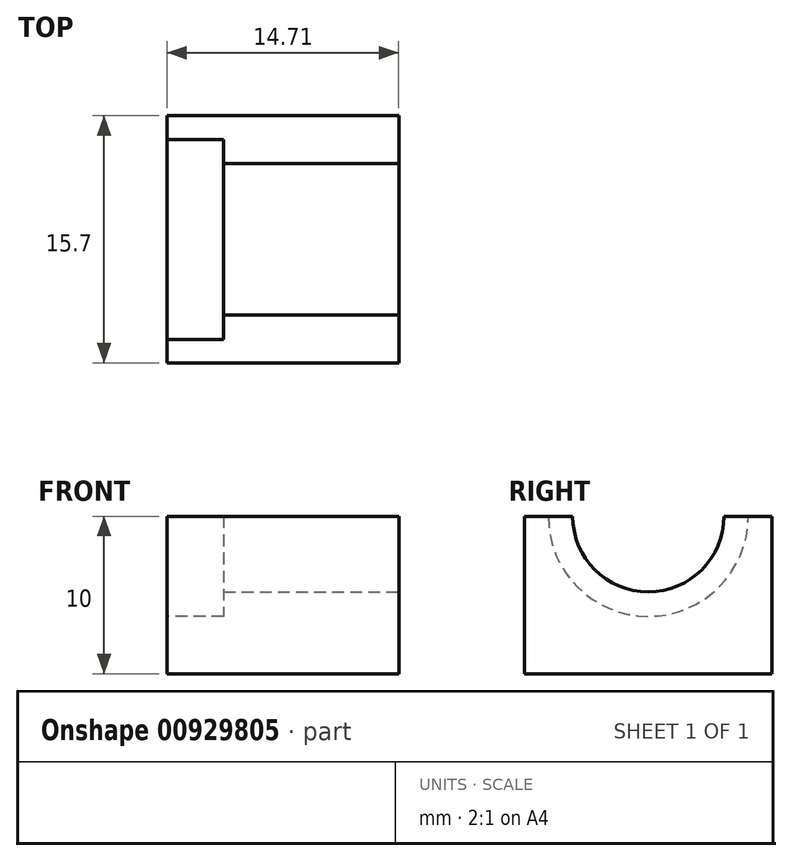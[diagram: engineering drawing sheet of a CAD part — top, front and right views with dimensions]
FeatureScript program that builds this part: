
annotation { "Feature Type Name" : "Feature", "Feature Type Description" : "" }
export const myFeature = defineFeature(function(context is Context, id is Id, definition is map)
    precondition{}
    {
        {
            var Q0;
            Q0=qCreatedBy(makeId("Front.planeOp"),FACE);
            var sketch = newSketch(context, id + "F0", { "sketchPlane" : qUnion([Q0])});
            skLineSegment(sketch, "E0", {"start": v(0, 0) * mm, "end": v(12.71, 0) * mm});
            skLineSegment(sketch, "E1", {"start": v(12.71, 0) * mm, "end": v(12.71, 20) * mm, "construction": true});
            skLineSegment(sketch, "E2", {"start": v(12.71, 20) * mm, "end": v(0, 20) * mm});
            skLineSegment(sketch, "E3", {"start": v(0, 20) * mm, "end": v(0, 17.5) * mm});
            skLineSegment(sketch, "E4", {"start": v(0, 17.5) * mm, "end": v(11.46, 17.5) * mm});
            skLineSegment(sketch, "E5", {"start": v(11.46, 17.5) * mm, "end": v(11.46, 2.5) * mm});
            skLineSegment(sketch, "E6", {"start": v(11.46, 2.5) * mm, "end": v(0, 2.5) * mm});
            skLineSegment(sketch, "E7", {"start": v(0, 2.5) * mm, "end": v(0, 0) * mm});
            skLineSegment(sketch, "E8.MirrorCS", {"start": v(12.71, 20) * mm, "end": v(25.43, 20) * mm});
            skLineSegment(sketch, "E9.MirrorCS", {"start": v(25.43, 20) * mm, "end": v(25.43, 17.5) * mm});
            skLineSegment(sketch, "E10.MirrorCS", {"start": v(25.43, 17.5) * mm, "end": v(13.96, 17.5) * mm});
            skLineSegment(sketch, "E11.MirrorCS", {"start": v(13.96, 17.5) * mm, "end": v(13.96, 2.5) * mm});
            skLineSegment(sketch, "E12.MirrorCS", {"start": v(13.96, 2.5) * mm, "end": v(25.43, 2.5) * mm});
            skLineSegment(sketch, "E13.MirrorCS", {"start": v(25.43, 2.5) * mm, "end": v(25.43, 0) * mm});
            skLineSegment(sketch, "E14.MirrorCS", {"start": v(25.43, 0) * mm, "end": v(12.71, 0) * mm});
            skSolve(sketch);
        }
        {
            var Q0;
            Q0=makeQuery(id+"F0.imprint","IMPRINT",FACE,{"disambiguationData":[TD([[makeQuery(id+"F0.imprint","IMPRINT",EDGE,{"derivedFrom":sQuery(id+"F0.wireOp",EDGE,"E0")}),1.0]])]});
            extrude(context, id + "F1", {"entities" : qUnion([Q0]), "oppositeDirection" : true, "depth" : 145 * mm, "offsetDistance" : 25 * mm});
        }
        {
            var Q0;
            Q0=makeQuery(id+"F1.opExtrude","SWEPT_FACE",FACE,{"disambiguationData":[OSD([sQuery(id+"F0.wireOp",EDGE,"E11.MirrorCS")])]});
            var sketch = newSketch(context, id + "F2", { "sketchPlane" : qUnion([Q0])});
            skLineSegment(sketch, "E15.bottom", {"start": v(0, 17.5) * mm, "end": v(15.7, 17.5) * mm});
            skLineSegment(sketch, "E15.top", {"start": v(0, 2.5) * mm, "end": v(15.7, 2.5) * mm});
            skLineSegment(sketch, "E15.left", {"start": v(0, 17.5) * mm, "end": v(0, 2.5) * mm});
            skLineSegment(sketch, "E15.right", {"start": v(15.7, 17.5) * mm, "end": v(15.7, 2.5) * mm});
            skSolve(sketch);
        }
        {
            var Q0;
            Q0=makeQuery(id+"F2.imprint","IMPRINT",FACE,{"disambiguationData":[TD([[makeQuery(id+"F2.imprint","IMPRINT",EDGE,{"derivedFrom":sQuery(id+"F2.wireOp",EDGE,"E15.bottom")}),1.0]])]});
            var Q1;
            Q1=makeQuery(id+"F1.opExtrude","SWEPT_FACE",FACE,{"disambiguationData":[OSD([sQuery(id+"F0.wireOp",EDGE,"E9.MirrorCS")])]});
            extrude(context, id + "F3", {"entities" : qUnion([Q0]), "operationType" : NewBodyOperationType.ADD, "endBound" : BoundingType.UP_TO_SURFACE, "depth" : 25 * mm, "endBoundEntityFace" : qUnion([Q1]), "offsetDistance" : 25 * mm});
        }
        {
            var Q0;
            Q0=makeQuery(id+"F1.opExtrude","SWEPT_FACE",FACE,{"disambiguationData":[OSD([sQuery(id+"F0.wireOp",EDGE,"E5")])]});
            var sketch = newSketch(context, id + "F4", { "sketchPlane" : qUnion([Q0])});
            skLineSegment(sketch, "E16.0", {"start": v(-15.7, 17.5) * mm, "end": v(-15.7, 2.5) * mm});
            skSolve(sketch);
        }
        {
            var Q0;
            {var subQ0=sQuery(id+"F4.wireOp",EDGE,"E16.0");Q0=makeQuery(id+"F4.imprint","IMPRINT",FACE,{"disambiguationData":[TD([[makeQuery(id+"F4.imprint","IMPRINT",EDGE,{"derivedFrom":subQ0}),1.0]])]});}
            var Q1;
            Q1=makeQuery(id+"F1.opExtrude","SWEPT_FACE",FACE,{"disambiguationData":[OSD([sQuery(id+"F0.wireOp",EDGE,"E3")])]});
            extrude(context, id + "F5", {"entities" : qUnion([Q0]), "operationType" : NewBodyOperationType.ADD, "endBound" : BoundingType.UP_TO_SURFACE, "depth" : 25 * mm, "endBoundEntityFace" : qUnion([Q1]), "offsetDistance" : 25 * mm});
        }
        {
            var Q0;
            Q0=makeQuery(id+"F3.boolean.opBoolean","MERGE",FACE,{"derivedFrom":[makeQuery(id+"F1.opExtrude","SWEPT_FACE",FACE,{"disambiguationData":[OSD([sQuery(id+"F0.wireOp",EDGE,"E9.MirrorCS")])]}),makeQuery(id+"F1.opExtrude","SWEPT_FACE",FACE,{"disambiguationData":[OSD([sQuery(id+"F0.wireOp",EDGE,"E13.MirrorCS")])]}),makeQuery(id+"F3.opExtrude","CAP_FACE",FACE,{"disambiguationData":[OSD([sQuery(id+"F2.wireOp",EDGE,"E15.bottom"),sQuery(id+"F2.wireOp",EDGE,"E15.top"),sQuery(id+"F2.wireOp",EDGE,"E15.left"),sQuery(id+"F2.wireOp",EDGE,"E15.right")])],"isStart":false})]});
            var sketch = newSketch(context, id + "F6", { "sketchPlane" : qUnion([Q0])});
            skLineSegment(sketch, "E17", {"start": v(0, 10) * mm, "end": v(15.7, 10) * mm});
            skCircle(sketch, "E18", {"center": v(7.85, 10) * mm, "radius": 4.8 * mm});
            skSolve(sketch);
        }
        {
            var Q0;
            {var subQ0=sQuery(id+"F6.wireOp",EDGE,"E18");var subQ1=sQuery(id+"F6.wireOp",EDGE,"E17");var subQ2=makeQuery(id+"F6.imprint","INTERSECT",VERTEX,{"disambiguationData":[OD(0.0)],"derivedFrom":[subQ1,subQ0]});Q0=makeQuery(id+"F6.imprint","IMPRINT",FACE,{"disambiguationData":[TD([[makeQuery(id+"F6.imprint","IMPRINT",EDGE,{"disambiguationData":[TD([[subQ2,-1.0]])],"derivedFrom":subQ1}),1.0]])]});}
            var Q1;
            {var subQ0=sQuery(id+"F6.wireOp",EDGE,"E18");var subQ1=sQuery(id+"F6.wireOp",EDGE,"E17");var subQ2=makeQuery(id+"F6.imprint","INTERSECT",VERTEX,{"disambiguationData":[OD(0.0)],"derivedFrom":[subQ1,subQ0]});Q1=makeQuery(id+"F6.imprint","IMPRINT",FACE,{"disambiguationData":[TD([[makeQuery(id+"F6.imprint","IMPRINT",EDGE,{"disambiguationData":[TD([[subQ2,-1.0]])],"derivedFrom":subQ1}),-1.0]])]});}
            extrude(context, id + "F7", {"entities" : qUnion([Q0, Q1]), "operationType" : NewBodyOperationType.REMOVE, "endBound" : BoundingType.THROUGH_ALL, "oppositeDirection" : true, "depth" : 1.2 * mm, "offsetDistance" : 25 * mm});
        }
        {
            var Q0;
            Q0=makeQuery(id+"F3.boolean.opBoolean","MERGE",FACE,{"derivedFrom":[makeQuery(id+"F1.opExtrude","SWEPT_FACE",FACE,{"disambiguationData":[OSD([sQuery(id+"F0.wireOp",EDGE,"E9.MirrorCS")])]}),makeQuery(id+"F1.opExtrude","SWEPT_FACE",FACE,{"disambiguationData":[OSD([sQuery(id+"F0.wireOp",EDGE,"E13.MirrorCS")])]}),makeQuery(id+"F3.opExtrude","CAP_FACE",FACE,{"disambiguationData":[OSD([sQuery(id+"F2.wireOp",EDGE,"E15.bottom"),sQuery(id+"F2.wireOp",EDGE,"E15.top"),sQuery(id+"F2.wireOp",EDGE,"E15.left"),sQuery(id+"F2.wireOp",EDGE,"E15.right")])],"isStart":false})]});
            var sketch = newSketch(context, id + "F8", { "sketchPlane" : qUnion([Q0])});
            skCircle(sketch, "E19", {"center": v(7.85, 10) * mm, "radius": 6.35 * mm});
            skSolve(sketch);
        }
        {
            var Q0;
            Q0=makeQuery(id+"F8.imprint","IMPRINT",FACE,{"disambiguationData":[TD([[makeQuery(id+"F8.imprint","IMPRINT",EDGE,{"derivedFrom":sQuery(id+"F8.wireOp",EDGE,"E19")}),1.0]])]});
            extrude(context, id + "F9", {"entities" : qUnion([Q0]), "operationType" : NewBodyOperationType.REMOVE, "oppositeDirection" : true, "depth" : 1.59 * mm, "offsetDistance" : 25 * mm});
        }
        {
            var Q0;
            Q0=makeQuery(id+"F6Z2DsxWZaRMq57_1.boolean.opBoolean","MERGE",FACE,{"derivedFrom":[makeQuery(id+"FBn6fwCzl5IuJvG_1.boolean.opBoolean","MERGE",FACE,{"derivedFrom":[makeQuery(id+"F5.boolean.opBoolean","MERGE",FACE,{"derivedFrom":[makeQuery(id+"F1.opExtrude","SWEPT_FACE",FACE,{"disambiguationData":[OSD([sQuery(id+"F0.wireOp",EDGE,"E3")])]}),makeQuery(id+"F1.opExtrude","SWEPT_FACE",FACE,{"disambiguationData":[OSD([sQuery(id+"F0.wireOp",EDGE,"E7")])]}),makeQuery(id+"F5.opExtrude","CAP_FACE",FACE,{"disambiguationData":[OSD([sQuery(id+"F0.wireOp",EDGE,"E4"),sQuery(id+"F0.wireOp",EDGE,"E5"),sQuery(id+"F0.wireOp",EDGE,"E6"),sQuery(id+"F4.wireOp",EDGE,"E16.0")])],"isStart":false})]}),makeQuery(id+"FBn6fwCzl5IuJvG_1.opExtrude","CAP_FACE",FACE,{"disambiguationData":[OSD([sQuery(id+"FJYeQwiUGTasUVH_1.wireOp",EDGE,"17f24a80-f7c9-426a-9816-c71a320d38ed.0"),sQuery(id+"FJYeQwiUGTasUVH_1.wireOp",EDGE,"17f24a80-f7c9-426a-9816-c71a320d38ed.1"),sQuery(id+"FJYeQwiUGTasUVH_1.wireOp",EDGE,"17f24a80-f7c9-426a-9816-c71a320d38ed.2"),sQuery(id+"FJYeQwiUGTasUVH_1.wireOp",EDGE,"17f24a80-f7c9-426a-9816-c71a320d38ed.3"),sQuery(id+"FJYeQwiUGTasUVH_1.wireOp",EDGE,"17f24a80-f7c9-426a-9816-c71a320d38ed.4"),sQuery(id+"FJYeQwiUGTasUVH_1.wireOp",EDGE,"17f24a80-f7c9-426a-9816-c71a320d38ed.5"),sQuery(id+"FJYeQwiUGTasUVH_1.wireOp",EDGE,"17f24a80-f7c9-426a-9816-c71a320d38ed.6"),sQuery(id+"FJYeQwiUGTasUVH_1.wireOp",EDGE,"17f24a80-f7c9-426a-9816-c71a320d38ed.7")])],"isStart":false})]}),makeQuery(id+"F6Z2DsxWZaRMq57_1.opExtrude","SWEPT_FACE",FACE,{"disambiguationData":[OSD([sQuery(id+"FydgGVjXTD0cEpR_1.wireOp",EDGE,"IIBRtL7t-InC5-384g-sMeV-U47FUIFXrSFr.left")])]})]});
            var sketch = newSketch(context, id + "F10", { "sketchPlane" : qUnion([Q0])});
            skCircle(sketch, "E20", {"center": v(-7.85, 10) * mm, "radius": 6.35 * mm});
            skSolve(sketch);
        }
        {
            var Q0;
            Q0=makeQuery(id+"F10.imprint","IMPRINT",FACE,{"disambiguationData":[TD([[makeQuery(id+"F10.imprint","IMPRINT",EDGE,{"derivedFrom":sQuery(id+"F10.wireOp",EDGE,"E20")}),1.0]])]});
            extrude(context, id + "F11", {"entities" : qUnion([Q0]), "operationType" : NewBodyOperationType.REMOVE, "oppositeDirection" : true, "depth" : 1.59 * mm, "offsetDistance" : 25 * mm});
        }
        {
            var Q0;
            Q0=makeQuery(id+"F3.boolean.opBoolean","MERGE",FACE,{"derivedFrom":[makeQuery(id+"F1.opExtrude","SWEPT_FACE",FACE,{"disambiguationData":[OSD([sQuery(id+"F0.wireOp",EDGE,"E9.MirrorCS")])]}),makeQuery(id+"F1.opExtrude","SWEPT_FACE",FACE,{"disambiguationData":[OSD([sQuery(id+"F0.wireOp",EDGE,"E13.MirrorCS")])]}),makeQuery(id+"F3.opExtrude","CAP_FACE",FACE,{"disambiguationData":[OSD([sQuery(id+"F2.wireOp",EDGE,"E15.bottom"),sQuery(id+"F2.wireOp",EDGE,"E15.top"),sQuery(id+"F2.wireOp",EDGE,"E15.left"),sQuery(id+"F2.wireOp",EDGE,"E15.right")])],"isStart":false})]});
            var sketch = newSketch(context, id + "F12", { "sketchPlane" : qUnion([Q0])});
            skLineSegment(sketch, "E21.bottom", {"start": v(15.7, 20) * mm, "end": v(145, 20) * mm});
            skLineSegment(sketch, "E21.top", {"start": v(15.7, 0) * mm, "end": v(145, 0) * mm});
            skLineSegment(sketch, "E21.left", {"start": v(15.7, 20) * mm, "end": v(15.7, 0) * mm});
            skLineSegment(sketch, "E21.right", {"start": v(145, 20) * mm, "end": v(145, 0) * mm});
            skSolve(sketch);
        }
        {
            var Q0;
            {var subQ0=sQuery(id+"F12.wireOp",EDGE,"E21.bottom");Q0=makeQuery(id+"F12.imprint","IMPRINT",FACE,{"disambiguationData":[TD([[makeQuery(id+"F12.imprint","IMPRINT",EDGE,{"derivedFrom":subQ0}),1.0]])]});}
            var Q1;
            {var subQ1=makeQuery(id+"F1.opExtrude","SWEPT_EDGE",EDGE,{"disambiguationData":[OSD([sQuery(id+"F0.wireOp",EDGE,"E9.MirrorCS"),sQuery(id+"F0.wireOp",EDGE,"E10.MirrorCS")])]});Q1=makeQuery(id+"F12.imprint","IMPRINT",FACE,{"disambiguationData":[TD([[makeQuery(id+"F12.imprint","IMPRINT",EDGE,{"derivedFrom":subQ1}),1.0]])]});}
            var Q2;
            {var subQ0=sQuery(id+"F12.wireOp",EDGE,"E21.top");Q2=makeQuery(id+"F12.imprint","IMPRINT",FACE,{"disambiguationData":[TD([[makeQuery(id+"F12.imprint","IMPRINT",EDGE,{"derivedFrom":subQ0}),-1.0]])]});}
            extrude(context, id + "F13", {"entities" : qUnion([Q0, Q1, Q2]), "operationType" : NewBodyOperationType.REMOVE, "endBound" : BoundingType.THROUGH_ALL, "oppositeDirection" : true, "depth" : 25 * mm, "offsetDistance" : 25 * mm});
        }
        {
            var Q0;
            Q0=makeQuery(id+"F5.boolean.opBoolean","MERGE",FACE,{"derivedFrom":[makeQuery(id+"F1.opExtrude","SWEPT_FACE",FACE,{"disambiguationData":[OSD([sQuery(id+"F0.wireOp",EDGE,"E3")])]}),makeQuery(id+"F1.opExtrude","SWEPT_FACE",FACE,{"disambiguationData":[OSD([sQuery(id+"F0.wireOp",EDGE,"E7")])]}),makeQuery(id+"F5.opExtrude","CAP_FACE",FACE,{"disambiguationData":[OSD([sQuery(id+"F0.wireOp",EDGE,"E4"),sQuery(id+"F0.wireOp",EDGE,"E5"),sQuery(id+"F0.wireOp",EDGE,"E6"),sQuery(id+"F4.wireOp",EDGE,"E16.0")])],"isStart":false})]});
            var sketch = newSketch(context, id + "F14", { "sketchPlane" : qUnion([Q0])});
            skLineSegment(sketch, "E22.bottom", {"start": v(-15.7, 10) * mm, "end": v(0, 10) * mm});
            skLineSegment(sketch, "E22.top", {"start": v(-15.7, 20) * mm, "end": v(0, 20) * mm});
            skLineSegment(sketch, "E22.left", {"start": v(-15.7, 10) * mm, "end": v(-15.7, 20) * mm});
            skLineSegment(sketch, "E22.right", {"start": v(0, 10) * mm, "end": v(0, 20) * mm});
            skSolve(sketch);
        }
        {
            var Q0;
            Q0=makeQuery(id+"F14.imprint","IMPRINT",FACE,{"disambiguationData":[TD([[makeQuery(id+"F14.imprint","IMPRINT",EDGE,{"derivedFrom":sQuery(id+"F14.wireOp",EDGE,"E22.top")}),-1.0]])]});
            var Q1;
            {var subQ0=sQuery(id+"F14.wireOp",EDGE,"E22.bottom");var subQ1=makeQuery(id+"F11.boolean.opBoolean","COPY",EDGE,{"derivedFrom":makeQuery(id+"F11.opExtrude","CAP_EDGE",EDGE,{"disambiguationData":[OSD([sQuery(id+"F10.wireOp",EDGE,"E20")])],"isStart":true})});var subQ2=makeQuery(id+"F14.imprint","INTERSECT",VERTEX,{"disambiguationData":[OD(0.0)],"derivedFrom":[subQ1,subQ0]});Q1=makeQuery(id+"F14.imprint","IMPRINT",FACE,{"disambiguationData":[TD([[makeQuery(id+"F14.imprint","IMPRINT",EDGE,{"disambiguationData":[TD([[subQ2,-1.0]])],"derivedFrom":subQ0}),1.0]])]});}
            extrude(context, id + "F15", {"entities" : qUnion([Q0, Q1]), "operationType" : NewBodyOperationType.REMOVE, "endBound" : BoundingType.THROUGH_ALL, "oppositeDirection" : true, "depth" : 25 * mm, "offsetDistance" : 25 * mm});
        }
        {
            var Q0;
            {var subQ0=sQuery(id+"F0.wireOp",EDGE,"E5");Q0=makeQuery(id+"F5.boolean.opBoolean","MERGE",FACE,{"derivedFrom":[makeQuery(id+"F3.boolean.opBoolean","MERGE",FACE,{"derivedFrom":[makeQuery(id+"F1.opExtrude","CAP_FACE",FACE,{"disambiguationData":[OSD([sQuery(id+"F0.wireOp",EDGE,"E0"),sQuery(id+"F0.wireOp",EDGE,"E2"),sQuery(id+"F0.wireOp",EDGE,"E3"),sQuery(id+"F0.wireOp",EDGE,"E4"),subQ0,sQuery(id+"F0.wireOp",EDGE,"E6"),sQuery(id+"F0.wireOp",EDGE,"E7"),sQuery(id+"F0.wireOp",EDGE,"E8.MirrorCS"),sQuery(id+"F0.wireOp",EDGE,"E9.MirrorCS"),sQuery(id+"F0.wireOp",EDGE,"E10.MirrorCS"),sQuery(id+"F0.wireOp",EDGE,"E11.MirrorCS"),sQuery(id+"F0.wireOp",EDGE,"E12.MirrorCS"),sQuery(id+"F0.wireOp",EDGE,"E13.MirrorCS"),sQuery(id+"F0.wireOp",EDGE,"E14.MirrorCS")])],"isStart":true}),makeQuery(id+"F3.opExtrude","SWEPT_FACE",FACE,{"disambiguationData":[OSD([sQuery(id+"F2.wireOp",EDGE,"E15.left")])]})]}),makeQuery(id+"F5.opExtrude","SWEPT_FACE",FACE,{"disambiguationData":[OSD([subQ0])]})]});}
            var sketch = newSketch(context, id + "F16", { "sketchPlane" : qUnion([Q0])});
            skLineSegment(sketch, "E23.bottom", {"start": v(12.71, 10) * mm, "end": v(25.43, 10) * mm});
            skLineSegment(sketch, "E23.top", {"start": v(12.71, 0) * mm, "end": v(25.43, 0) * mm});
            skLineSegment(sketch, "E23.left", {"start": v(12.71, 10) * mm, "end": v(12.71, 0) * mm});
            skLineSegment(sketch, "E23.right", {"start": v(25.43, 10) * mm, "end": v(25.43, 0) * mm});
            skSolve(sketch);
        }
        {
            var Q0;
            Q0=makeQuery(id+"F16.imprint","IMPRINT",FACE,{"disambiguationData":[TD([[makeQuery(id+"F16.imprint","IMPRINT",EDGE,{"derivedFrom":sQuery(id+"F16.wireOp",EDGE,"E23.bottom")}),1.0]])]});
            extrude(context, id + "F17", {"entities" : qUnion([Q0]), "operationType" : NewBodyOperationType.REMOVE, "endBound" : BoundingType.THROUGH_ALL, "oppositeDirection" : true, "depth" : 25 * mm, "offsetDistance" : 25 * mm});
        }
        {
            var Q0;
            Q0=makeQuery(id+"F5.boolean.opBoolean","MERGE",FACE,{"derivedFrom":[makeQuery(id+"F1.opExtrude","SWEPT_FACE",FACE,{"disambiguationData":[OSD([sQuery(id+"F0.wireOp",EDGE,"E3")])]}),makeQuery(id+"F1.opExtrude","SWEPT_FACE",FACE,{"disambiguationData":[OSD([sQuery(id+"F0.wireOp",EDGE,"E7")])]}),makeQuery(id+"F5.opExtrude","CAP_FACE",FACE,{"disambiguationData":[OSD([sQuery(id+"F0.wireOp",EDGE,"E4"),sQuery(id+"F0.wireOp",EDGE,"E5"),sQuery(id+"F0.wireOp",EDGE,"E6"),sQuery(id+"F4.wireOp",EDGE,"E16.0")])],"isStart":false})]});
            var sketch = newSketch(context, id + "F18", { "sketchPlane" : qUnion([Q0])});
            skLineSegment(sketch, "E24.bottom", {"start": v(-15.7, 10) * mm, "end": v(0, 10) * mm});
            skLineSegment(sketch, "E24.top", {"start": v(-15.7, 0) * mm, "end": v(0, 0) * mm});
            skLineSegment(sketch, "E24.left", {"start": v(-15.7, 10) * mm, "end": v(-15.7, 0) * mm});
            skLineSegment(sketch, "E24.right", {"start": v(0, 10) * mm, "end": v(0, 0) * mm});
            skSolve(sketch);
        }
        {
            var Q0;
            {var subQ1=makeQuery(id+"F11.boolean.opBoolean","COPY",EDGE,{"derivedFrom":makeQuery(id+"F11.opExtrude","CAP_EDGE",EDGE,{"disambiguationData":[OSD([sQuery(id+"F10.wireOp",EDGE,"E20")])],"isStart":true})});Q0=makeQuery(id+"F18.imprint","IMPRINT",FACE,{"disambiguationData":[TD([[makeQuery(id+"F18.imprint","IMPRINT",EDGE,{"derivedFrom":subQ1}),1.0]])]});}
            var Q1;
            Q1=makeQuery(id+"F18.imprint","IMPRINT",FACE,{"disambiguationData":[TD([[makeQuery(id+"F18.imprint","IMPRINT",EDGE,{"derivedFrom":sQuery(id+"F18.wireOp",EDGE,"E24.top")}),1.0]])]});
            extrude(context, id + "F19", {"entities" : qUnion([Q0, Q1]), "operationType" : NewBodyOperationType.ADD, "depth" : 2 * mm, "offsetDistance" : 25 * mm});
        }
    });
